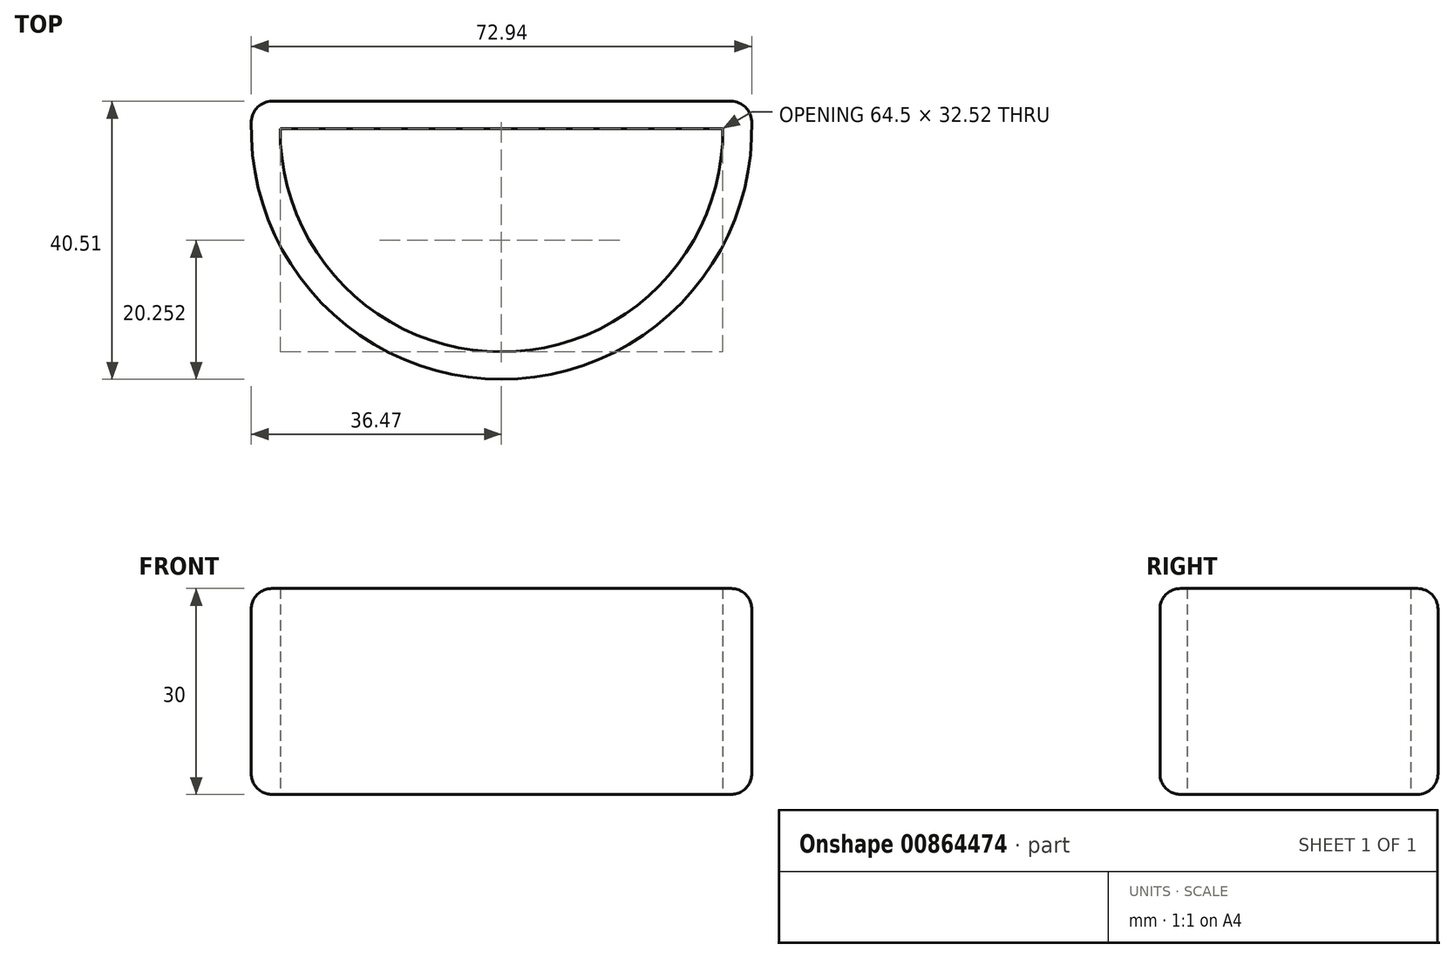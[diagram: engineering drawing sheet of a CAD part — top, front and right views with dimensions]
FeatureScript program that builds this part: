
annotation { "Feature Type Name" : "Feature", "Feature Type Description" : "" }
export const myFeature = defineFeature(function(context is Context, id is Id, definition is map)
    precondition{}
    {
        {
            var Q0;
            Q0=qCreatedBy(makeId("Top.planeOp"),FACE);
            var sketch = newSketch(context, id + "F0", { "sketchPlane" : qUnion([Q0])});
            skArc(sketch, "E0", {"start": v(-33.25, 32.5) * mm, "mid": v(-1, -0.02) * mm, "end": v(31.25, 32.5) * mm});
            skLineSegment(sketch, "E1", {"start": v(0, 0) * mm, "end": v(0, -4) * mm});
            skArc(sketch, "E2", {"start": v(-37.25, 36.5) * mm, "mid": v(-1, -4.01) * mm, "end": v(35.25, 36.5) * mm});
            skLineSegment(sketch, "E3", {"start": v(-33.25, 32.5) * mm, "end": v(31.25, 32.5) * mm});
            skLineSegment(sketch, "E4", {"start": v(-37.25, 36.5) * mm, "end": v(35.25, 36.5) * mm});
            skSolve(sketch);
        }
        {
            var Q0;
            {var subQ3=sQuery(id+"F0.wireOp",EDGE,"E3");Q0=makeQuery(id+"F0.imprint","IMPRINT",FACE,{"disambiguationData":[TD([[makeQuery(id+"F0.imprint","IMPRINT",EDGE,{"derivedFrom":subQ3}),1.0]])]});}
            extrude(context, id + "F1", {"entities" : qUnion([Q0]), "depth" : 30 * mm, "offsetDistance" : 25 * mm});
        }
        {
            var Q0;
            Q0=makeQuery(id+"F1.opExtrude","CAP_EDGE",EDGE,{"disambiguationData":[OSD([sQuery(id+"F0.wireOp",EDGE,"E2")])],"isStart":false});
            var Q1;
            Q1=makeQuery(id+"F1.opExtrude","CAP_EDGE",EDGE,{"disambiguationData":[OSD([sQuery(id+"F0.wireOp",EDGE,"E4")])],"isStart":false});
            fillet(context, id + "F2", {"entities" : qUnion([Q0, Q1]), "radius" : 3 * mm, "tangentPropagation" : true, "allowEdgeOverflow" : false});
        }
        {
            var Q0;
            Q0=makeQuery(id+"F1.opExtrude","CAP_EDGE",EDGE,{"disambiguationData":[OSD([sQuery(id+"F0.wireOp",EDGE,"E4")])],"isStart":true});
            var Q1;
            Q1=makeQuery(id+"F1.opExtrude","CAP_EDGE",EDGE,{"disambiguationData":[OSD([sQuery(id+"F0.wireOp",EDGE,"E2")])],"isStart":true});
            var Q2;
            {var subQ0=sQuery(id+"F0.wireOp",EDGE,"E4");var subQ1=sQuery(id+"F0.wireOp",EDGE,"E2");Q2=makeQuery(id+"F1.opExtrude","SWEPT_EDGE",EDGE,{"disambiguationData":[OSD([subQ1,subQ0]),TDD([makeQuery(id+"F0.imprint","INTERSECT",VERTEX,{"disambiguationData":[OD(1.0)],"derivedFrom":[subQ1,subQ0]})])]});}
            var Q3;
            {var subQ0=sQuery(id+"F0.wireOp",EDGE,"E4");var subQ1=sQuery(id+"F0.wireOp",EDGE,"E2");Q3=makeQuery(id+"F1.opExtrude","SWEPT_EDGE",EDGE,{"disambiguationData":[OSD([subQ1,subQ0]),TDD([makeQuery(id+"F0.imprint","INTERSECT",VERTEX,{"disambiguationData":[OD(0.0)],"derivedFrom":[subQ1,subQ0]})])]});}
            fillet(context, id + "F3", {"entities" : qUnion([Q0, Q1, Q2, Q3]), "radius" : 3 * mm, "tangentPropagation" : true, "allowEdgeOverflow" : false});
        }
    });
